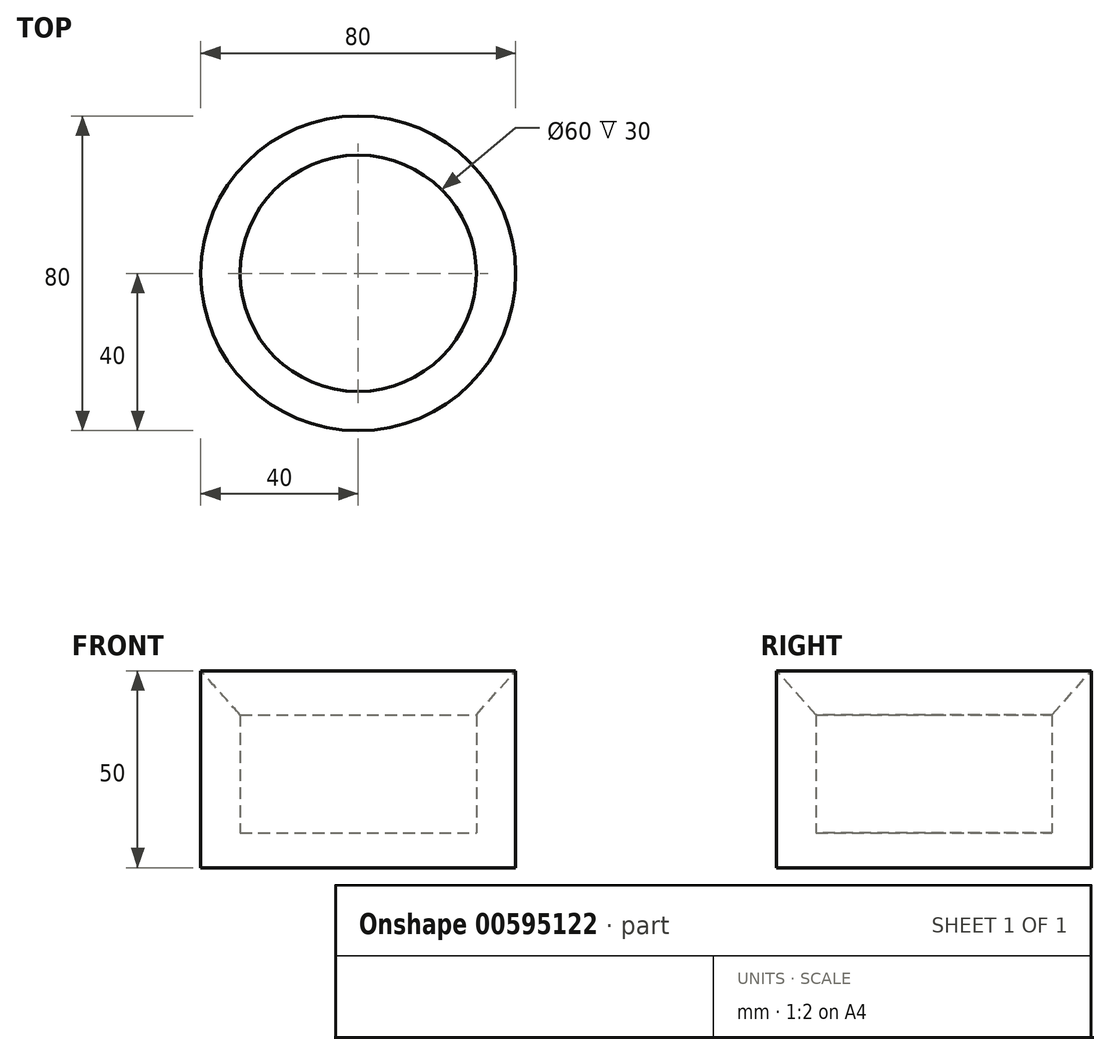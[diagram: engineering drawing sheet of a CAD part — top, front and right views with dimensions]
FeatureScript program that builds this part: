
annotation { "Feature Type Name" : "Feature", "Feature Type Description" : "" }
export const myFeature = defineFeature(function(context is Context, id is Id, definition is map)
    precondition{}
    {
        {
            var Q0;
            Q0=qCreatedBy(makeId("Front.planeOp"),FACE);
            var sketch = newSketch(context, id + "F0", { "sketchPlane" : qUnion([Q0])});
            skLineSegment(sketch, "E0", {"start": v(-40, 41.18) * mm, "end": v(-40, -8.82) * mm});
            skLineSegment(sketch, "E1", {"start": v(-40, -8.82) * mm, "end": v(0, -8.82) * mm});
            skLineSegment(sketch, "E2", {"start": v(0, -8.82) * mm, "end": v(0, 0) * mm});
            skLineSegment(sketch, "E3", {"start": v(0, 0) * mm, "end": v(-30, 0) * mm});
            skLineSegment(sketch, "E4", {"start": v(-30, 0) * mm, "end": v(-30, 30) * mm});
            skLineSegment(sketch, "E5", {"start": v(-30, 30) * mm, "end": v(-40, 41.18) * mm});
            skSolve(sketch);
        }
        {
            var Q0;
            Q0=makeQuery(id+"F0.imprint","IMPRINT",FACE,{"disambiguationData":[TD([[makeQuery(id+"F0.imprint","IMPRINT",EDGE,{"derivedFrom":sQuery(id+"F0.wireOp",EDGE,"E0")}),1.0]])]});
            var Q1;
            Q1=sQuery(id+"F0.wireOp",EDGE,"E2");
            var Q2;
            Q2=sQuery(id+"F0.wireOp",EDGE,"E2");
            revolve(context, id + "F1", {"entities" : qUnion([Q0]), "surfaceEntities" : qUnion([Q1]), "axis" : qUnion([Q2]), "revolveType" : RevolveType.FULL});
        }
    });
